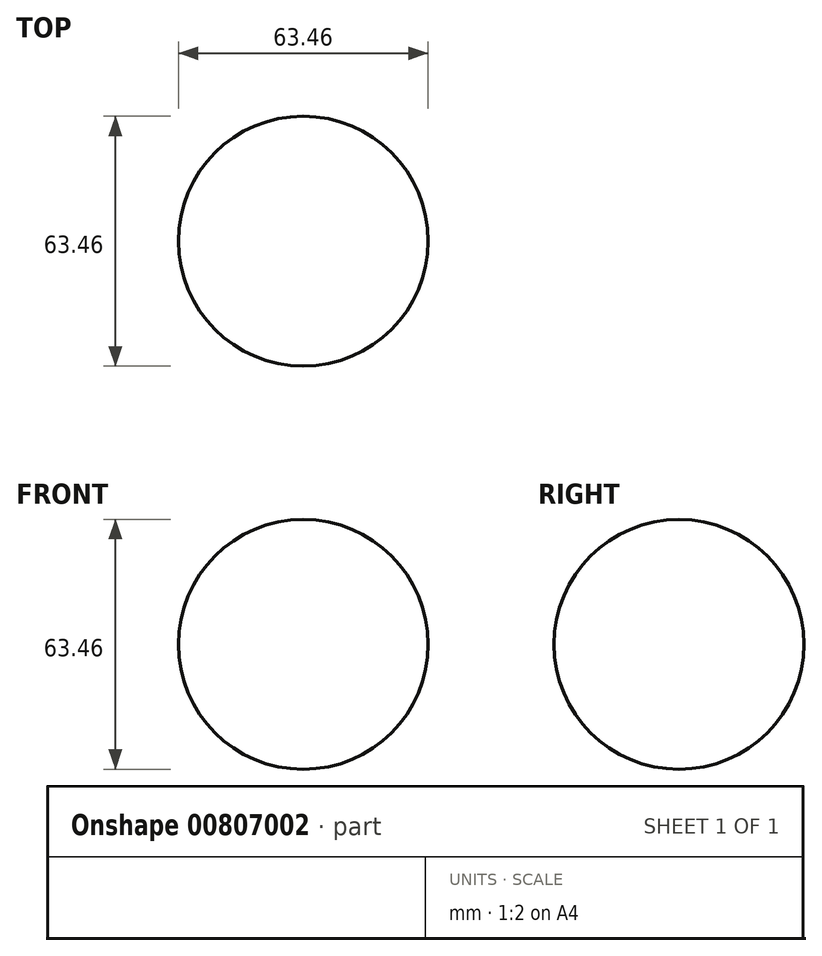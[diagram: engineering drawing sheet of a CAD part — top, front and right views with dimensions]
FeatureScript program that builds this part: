
annotation { "Feature Type Name" : "Feature", "Feature Type Description" : "" }
export const myFeature = defineFeature(function(context is Context, id is Id, definition is map)
    precondition{}
    {
        {
            var Q0;
            Q0=qCreatedBy(makeId("Front.planeOp"),FACE);
            var sketch = newSketch(context, id + "F0", { "sketchPlane" : qUnion([Q0])});
            skCircle(sketch, "E0", {"center": v(0, 0) * mm, "radius": 31.73 * mm});
            skLineSegment(sketch, "E1", {"start": v(0, 0) * mm, "end": v(0, 42.66) * mm});
            skLineSegment(sketch, "E2", {"start": v(0, 42.66) * mm, "end": v(0, -40.66) * mm});
            skSolve(sketch);
        }
        {
            var Q0;
            {var subQ0=sQuery(id+"F0.wireOp",EDGE,"E1");var subQ1=sQuery(id+"F0.wireOp",EDGE,"E0");var subQ2=makeQuery(id+"F0.imprint","INTERSECT",VERTEX,{"derivedFrom":[subQ1,subQ0]});Q0=makeQuery(id+"F0.imprint","IMPRINT",FACE,{"disambiguationData":[TD([[makeQuery(id+"F0.imprint","IMPRINT",EDGE,{"disambiguationData":[TD([[subQ2,-1.0]])],"derivedFrom":subQ1}),1.0]])]});}
            var Q1;
            Q1=sQuery(id+"F0.wireOp",EDGE,"E2");
            revolve(context, id + "F1", {"surfaceOperationType" : NewSurfaceOperationType.NEW, "entities" : qUnion([Q0]), "axis" : qUnion([Q1]), "revolveType" : RevolveType.FULL});
        }
    });
